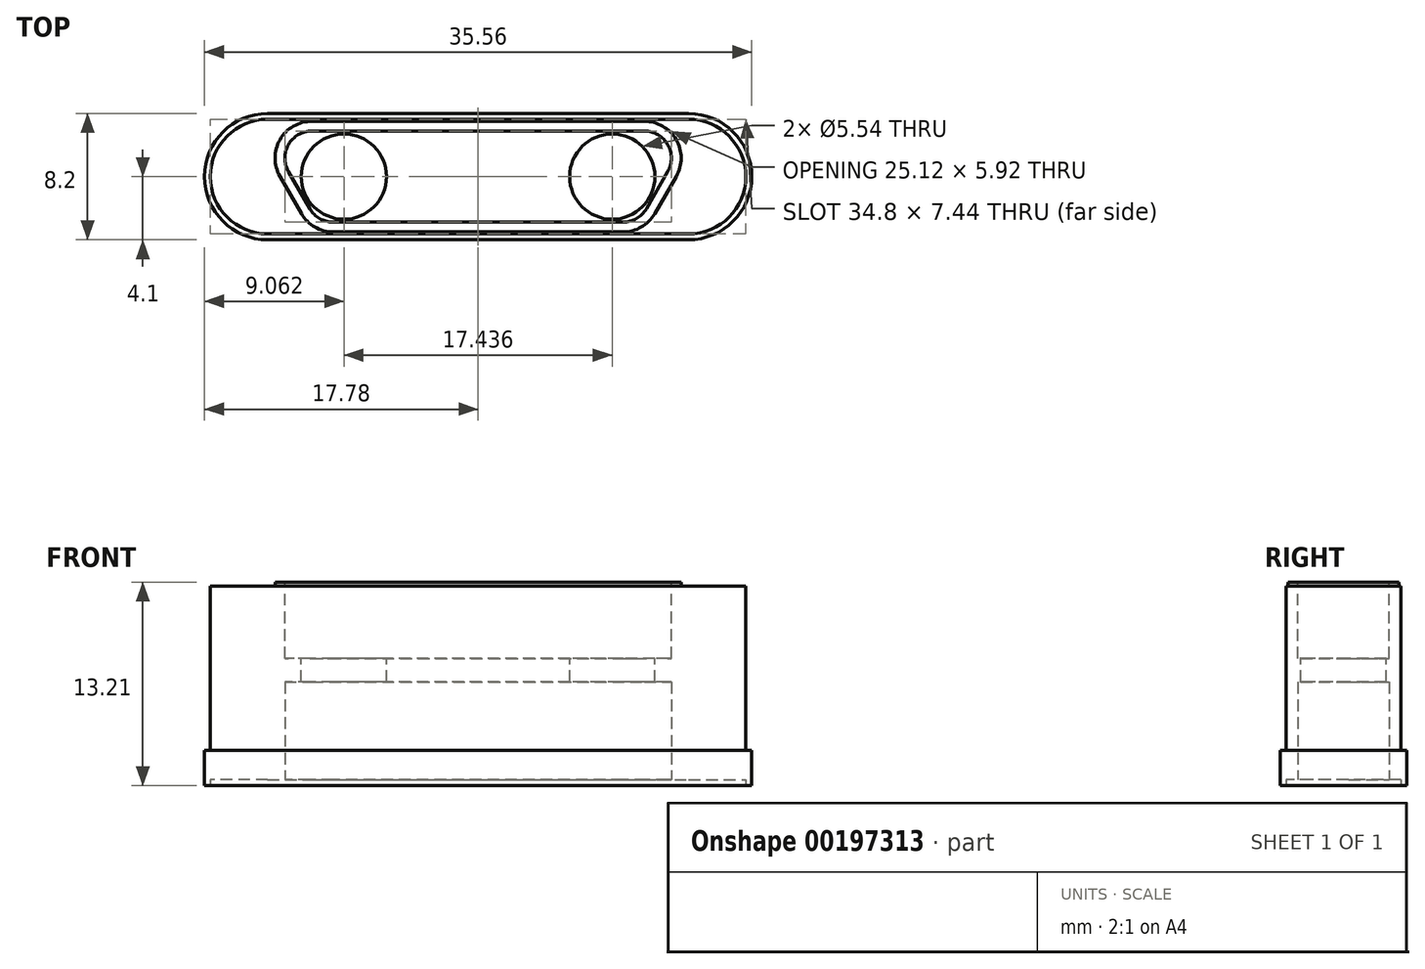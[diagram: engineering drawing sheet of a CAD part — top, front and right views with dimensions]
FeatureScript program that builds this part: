
annotation { "Feature Type Name" : "Feature", "Feature Type Description" : "" }
export const myFeature = defineFeature(function(context is Context, id is Id, definition is map)
    precondition{}
    {
        {
            var Q0;
            Q0=qCreatedBy(makeId("Top.planeOp"),FACE);
            var sketch = newSketch(context, id + "F0", { "sketchPlane" : qUnion([Q0])});
            skLineSegment(sketch, "E0", {"start": v(-15.43, 0) * mm, "end": v(15.43, 0) * mm, "construction": true});
            skLineSegment(sketch, "E1", {"start": v(0, 5.17) * mm, "end": v(0, -5.17) * mm, "construction": true});
            skArc(sketch, "E2", {"start": v(13.68, -4.1) * mm, "mid": v(17.78, 0) * mm, "end": v(13.68, 4.1) * mm});
            skArc(sketch, "E3", {"start": v(-13.68, 4.1) * mm, "mid": v(-17.78, 0) * mm, "end": v(-13.68, -4.1) * mm});
            skLineSegment(sketch, "E4", {"start": v(-13.68, 4.1) * mm, "end": v(13.68, 4.1) * mm});
            skLineSegment(sketch, "E5", {"start": v(-13.68, -4.1) * mm, "end": v(13.68, -4.1) * mm});
            skLineSegment(sketch, "E6.0", {"start": v(-13.68, 3.72) * mm, "end": v(13.68, 3.72) * mm});
            skArc(sketch, "E6.1", {"start": v(-13.68, 3.72) * mm, "mid": v(-17.4, 0) * mm, "end": v(-13.68, -3.72) * mm});
            skLineSegment(sketch, "E6.2", {"start": v(-13.68, -3.72) * mm, "end": v(13.68, -3.72) * mm});
            skArc(sketch, "E6.3", {"start": v(13.68, -3.72) * mm, "mid": v(17.4, 0) * mm, "end": v(13.68, 3.72) * mm});
            skLineSegment(sketch, "E7", {"start": v(-10.8, 2.96) * mm, "end": v(10.8, 2.96) * mm});
            skLineSegment(sketch, "E8", {"start": v(12.33, 0.33) * mm, "end": v(10.93, -2.08) * mm});
            skLineSegment(sketch, "E9", {"start": v(9.41, -2.96) * mm, "end": v(-9.41, -2.96) * mm});
            skLineSegment(sketch, "E10", {"start": v(-10.93, -2.08) * mm, "end": v(-12.33, 0.33) * mm});
            skArc(sketch, "E11.filletArc", {"start": v(-10.8, 2.96) * mm, "mid": v(-12.33, 2.08) * mm, "end": v(-12.33, 0.33) * mm});
            skArc(sketch, "E12.filletArc", {"start": v(12.33, 0.33) * mm, "mid": v(12.33, 2.08) * mm, "end": v(10.8, 2.96) * mm});
            skArc(sketch, "E13.filletArc", {"start": v(9.41, -2.96) * mm, "mid": v(10.3, -2.72) * mm, "end": v(10.93, -2.08) * mm});
            skArc(sketch, "E14.filletArc", {"start": v(-10.93, -2.08) * mm, "mid": v(-10.3, -2.72) * mm, "end": v(-9.41, -2.96) * mm});
            skArc(sketch, "E15.0", {"start": v(-10.8, 3.6) * mm, "mid": v(-12.88, 2.4) * mm, "end": v(-12.88, 0.01) * mm});
            skLineSegment(sketch, "E15.1", {"start": v(-11.48, -2.4) * mm, "end": v(-12.88, 0.01) * mm});
            skLineSegment(sketch, "E15.2", {"start": v(-10.8, 3.6) * mm, "end": v(10.8, 3.6) * mm});
            skArc(sketch, "E15.3", {"start": v(-11.48, -2.4) * mm, "mid": v(-10.6, -3.27) * mm, "end": v(-9.41, -3.6) * mm});
            skArc(sketch, "E15.4", {"start": v(12.88, 0.01) * mm, "mid": v(12.88, 2.4) * mm, "end": v(10.8, 3.6) * mm});
            skLineSegment(sketch, "E15.5", {"start": v(12.88, 0.01) * mm, "end": v(11.48, -2.4) * mm});
            skArc(sketch, "E15.6", {"start": v(9.41, -3.6) * mm, "mid": v(10.6, -3.27) * mm, "end": v(11.48, -2.4) * mm});
            skLineSegment(sketch, "E15.7", {"start": v(9.41, -3.6) * mm, "end": v(-9.41, -3.6) * mm});
            skCircle(sketch, "E16", {"center": v(-8.72, 0) * mm, "radius": 2.96 * mm, "construction": true});
            skCircle(sketch, "E17", {"center": v(8.72, 0) * mm, "radius": 2.96 * mm, "construction": true});
            skCircle(sketch, "E18", {"center": v(-8.72, 0) * mm, "radius": 2.77 * mm});
            skCircle(sketch, "E19", {"center": v(8.72, 0) * mm, "radius": 2.77 * mm});
            skSolve(sketch);
        }
        {
            var Q0;
            Q0=makeQuery(id+"F0.imprint","IMPRINT",FACE,{"disambiguationData":[TD([[makeQuery(id+"F0.imprint","IMPRINT",EDGE,{"derivedFrom":sQuery(id+"F0.wireOp",EDGE,"E2")}),1.0]])]});
            var Q1;
            Q1=makeQuery(id+"F0.imprint","IMPRINT",FACE,{"disambiguationData":[TD([[makeQuery(id+"F0.imprint","IMPRINT",EDGE,{"derivedFrom":sQuery(id+"F0.wireOp",EDGE,"E6.0")}),-1.0]])]});
            var Q2;
            Q2=makeQuery(id+"F0.imprint","IMPRINT",FACE,{"disambiguationData":[TD([[makeQuery(id+"F0.imprint","IMPRINT",EDGE,{"derivedFrom":sQuery(id+"F0.wireOp",EDGE,"E7")}),1.0]])]});
            var Q3;
            Q3=makeQuery(id+"F0.imprint","IMPRINT",FACE,{"disambiguationData":[TD([[makeQuery(id+"F0.imprint","IMPRINT",EDGE,{"derivedFrom":sQuery(id+"F0.wireOp",EDGE,"E7")}),-1.0]])]});
            extrude(context, id + "F1", {"entities" : qUnion([Q0, Q1, Q2, Q3]), "oppositeDirection" : true, "depth" : 13.2 * mm});
        }
        {
            var Q0;
            Q0=makeQuery(id+"F0.imprint","IMPRINT",FACE,{"disambiguationData":[TD([[makeQuery(id+"F0.imprint","IMPRINT",EDGE,{"derivedFrom":sQuery(id+"F0.wireOp",EDGE,"E2")}),1.0]])]});
            extrude(context, id + "F2", {"entities" : qUnion([Q0]), "operationType" : NewBodyOperationType.REMOVE, "oppositeDirection" : true, "depth" : 10.92 * mm});
        }
        {
            var Q0;
            Q0=makeQuery(id+"F0.imprint","IMPRINT",FACE,{"disambiguationData":[TD([[makeQuery(id+"F0.imprint","IMPRINT",EDGE,{"derivedFrom":sQuery(id+"F0.wireOp",EDGE,"E6.0")}),-1.0]])]});
            extrude(context, id + "F3", {"entities" : qUnion([Q0]), "operationType" : NewBodyOperationType.REMOVE, "oppositeDirection" : true, "depth" : 0.25 * mm});
        }
        {
            var Q0;
            Q0=makeQuery(id+"F0.imprint","IMPRINT",FACE,{"disambiguationData":[TD([[makeQuery(id+"F0.imprint","IMPRINT",EDGE,{"derivedFrom":sQuery(id+"F0.wireOp",EDGE,"E7")}),-1.0]])]});
            extrude(context, id + "F4", {"entities" : qUnion([Q0]), "operationType" : NewBodyOperationType.REMOVE, "oppositeDirection" : true, "depth" : 4.95 * mm});
        }
        {
            var Q0;
            Q0=makeQuery(id+"F1.opExtrude","CAP_FACE",FACE,{"disambiguationData":[OSD([sQuery(id+"F0.wireOp",EDGE,"E2"),sQuery(id+"F0.wireOp",EDGE,"E3"),sQuery(id+"F0.wireOp",EDGE,"E4"),sQuery(id+"F0.wireOp",EDGE,"E5")])],"isStart":false});
            var sketch = newSketch(context, id + "F5", { "sketchPlane" : qUnion([Q0])});
            skLineSegment(sketch, "E20.0", {"start": v(-10.8, -2.96) * mm, "end": v(10.8, -2.96) * mm});
            skArc(sketch, "E21.0", {"start": v(12.33, -0.33) * mm, "mid": v(12.33, -2.08) * mm, "end": v(10.8, -2.96) * mm});
            skLineSegment(sketch, "E22.0", {"start": v(12.33, -0.33) * mm, "end": v(10.93, 2.08) * mm});
            skArc(sketch, "E23.0", {"start": v(9.41, 2.96) * mm, "mid": v(10.3, 2.72) * mm, "end": v(10.93, 2.08) * mm});
            skLineSegment(sketch, "E24.0", {"start": v(9.41, 2.96) * mm, "end": v(-9.41, 2.96) * mm});
            skArc(sketch, "E25.0", {"start": v(-10.93, 2.08) * mm, "mid": v(-10.3, 2.72) * mm, "end": v(-9.41, 2.96) * mm});
            skLineSegment(sketch, "E26.0", {"start": v(-10.93, 2.08) * mm, "end": v(-12.33, -0.33) * mm});
            skArc(sketch, "E27.0", {"start": v(-10.8, -2.96) * mm, "mid": v(-12.33, -2.08) * mm, "end": v(-12.33, -0.33) * mm});
            skArc(sketch, "E28.0", {"start": v(13.68, 3.72) * mm, "mid": v(17.4, 0) * mm, "end": v(13.68, -3.72) * mm});
            skLineSegment(sketch, "E29.0", {"start": v(-13.68, -3.72) * mm, "end": v(13.68, -3.72) * mm});
            skLineSegment(sketch, "E30.0", {"start": v(-13.68, 3.72) * mm, "end": v(13.68, 3.72) * mm});
            skArc(sketch, "E31.0", {"start": v(-13.68, -3.72) * mm, "mid": v(-17.4, 0) * mm, "end": v(-13.68, 3.72) * mm});
            skLineSegment(sketch, "E32.0", {"start": v(-15.43, 0) * mm, "end": v(15.43, 0) * mm, "construction": true});
            skSolve(sketch);
        }
        {
            var Q0;
            Q0=makeQuery(id+"F5.imprint","IMPRINT",FACE,{"disambiguationData":[TD([[makeQuery(id+"F5.imprint","IMPRINT",EDGE,{"derivedFrom":sQuery(id+"F5.wireOp",EDGE,"E20.0")}),1.0]])]});
            extrude(context, id + "F6", {"entities" : qUnion([Q0]), "operationType" : NewBodyOperationType.REMOVE, "oppositeDirection" : true, "depth" : 6.73 * mm});
        }
        {
            var Q0;
            Q0=makeQuery(id+"F5.imprint","IMPRINT",FACE,{"disambiguationData":[TD([[makeQuery(id+"F5.imprint","IMPRINT",EDGE,{"derivedFrom":sQuery(id+"F5.wireOp",EDGE,"E20.0")}),-1.0]])]});
            extrude(context, id + "F7", {"entities" : qUnion([Q0]), "operationType" : NewBodyOperationType.REMOVE, "oppositeDirection" : true, "depth" : 0.38 * mm});
        }
    });
